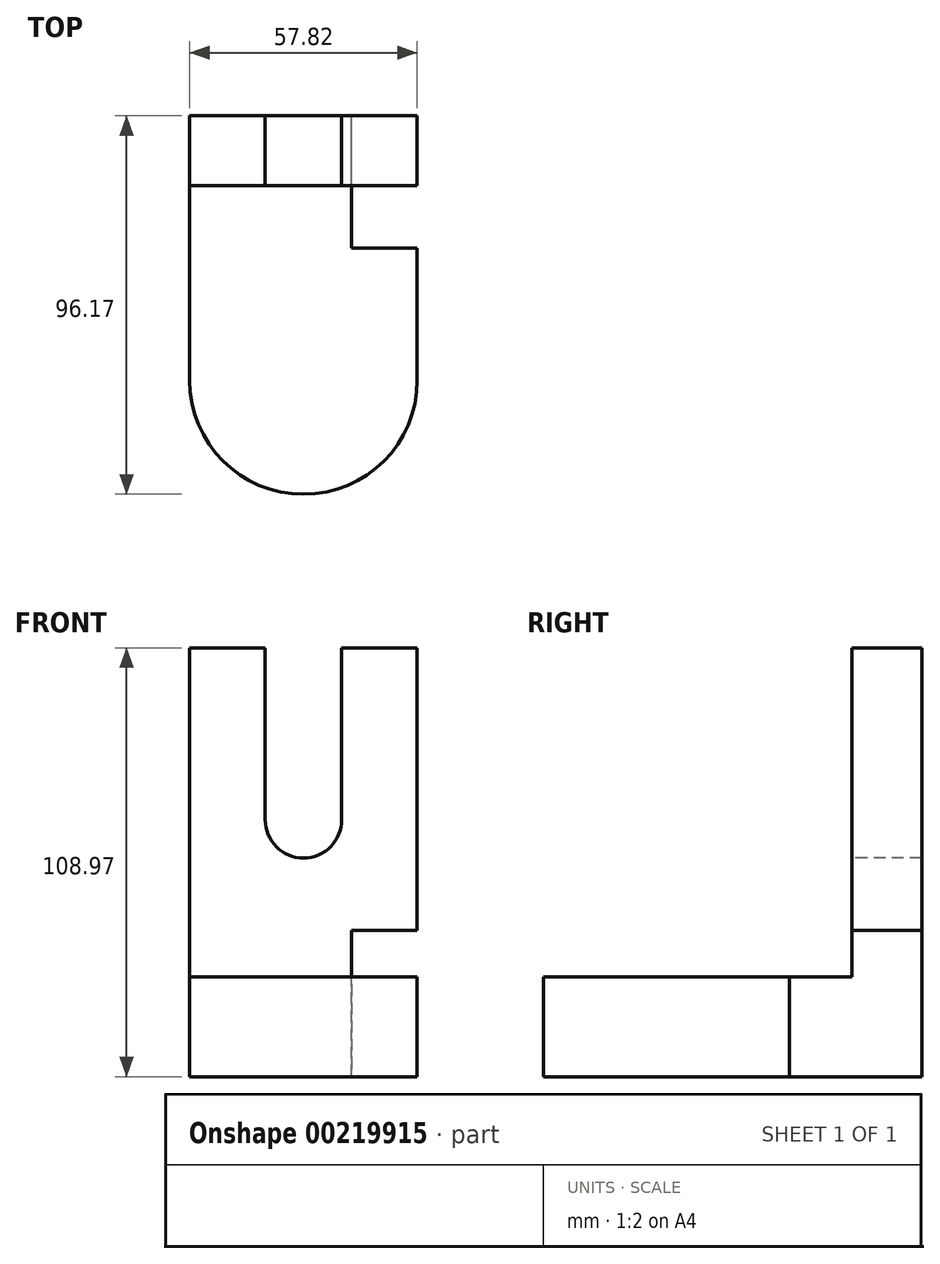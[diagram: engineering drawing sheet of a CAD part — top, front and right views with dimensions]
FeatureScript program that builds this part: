
annotation { "Feature Type Name" : "Feature", "Feature Type Description" : "" }
export const myFeature = defineFeature(function(context is Context, id is Id, definition is map)
    precondition{}
    {
        {
            var Q0;
            Q0=qCreatedBy(makeId("Top.planeOp"),FACE);
            var sketch = newSketch(context, id + "F0", { "sketchPlane" : qUnion([Q0])});
            skLineSegment(sketch, "E0.bottom", {"start": v(-28.91, -33.63) * mm, "end": v(28.91, -33.63) * mm});
            skLineSegment(sketch, "E0.top", {"start": v(-28.91, 33.63) * mm, "end": v(28.91, 33.63) * mm});
            skLineSegment(sketch, "E0.left", {"start": v(-28.91, -33.63) * mm, "end": v(-28.91, 33.63) * mm});
            skLineSegment(sketch, "E0.right", {"start": v(28.91, -33.63) * mm, "end": v(28.91, 33.63) * mm});
            skPoint(sketch, "E0.middle", {"position": v(0, 0) * mm});
            skSolve(sketch);
        }
        {
            var Q0;
            Q0 = qSketchRegion(id + "F0", true);
            extrude(context, id + "F1", {"entities" : qUnion([Q0]), "depth" : 25.4 * mm});
        }
        {
            var Q0;
            Q0=makeQuery(id+"F1.opExtrude","CAP_FACE",FACE,{"disambiguationData":[OSD([sQuery(id+"F0.wireOp",EDGE,"E0.bottom"),sQuery(id+"F0.wireOp",EDGE,"E0.top"),sQuery(id+"F0.wireOp",EDGE,"E0.left"),sQuery(id+"F0.wireOp",EDGE,"E0.right")])],"isStart":false});
            var sketch = newSketch(context, id + "F2", { "sketchPlane" : qUnion([Q0])});
            skLineSegment(sketch, "E1.bottom", {"start": v(-28.91, 33.63) * mm, "end": v(28.91, 33.63) * mm});
            skLineSegment(sketch, "E1.top", {"start": v(-28.91, 15.92) * mm, "end": v(28.91, 15.92) * mm});
            skLineSegment(sketch, "E1.left", {"start": v(-28.91, 33.63) * mm, "end": v(-28.91, 15.92) * mm});
            skLineSegment(sketch, "E1.right", {"start": v(28.91, 33.63) * mm, "end": v(28.91, 15.92) * mm});
            skSolve(sketch);
        }
        {
            var Q0;
            Q0 = qSketchRegion(id + "F2", true);
            extrude(context, id + "F3", {"entities" : qUnion([Q0]), "operationType" : NewBodyOperationType.ADD, "depth" : 83.57 * mm});
        }
        {
            var Q0;
            Q0=makeQuery(id+"F3.opExtrude","CAP_FACE",FACE,{"disambiguationData":[OSD([sQuery(id+"F2.wireOp",EDGE,"E1.bottom"),sQuery(id+"F2.wireOp",EDGE,"E1.top"),sQuery(id+"F2.wireOp",EDGE,"E1.left"),sQuery(id+"F2.wireOp",EDGE,"E1.right")])],"isStart":false});
            var sketch = newSketch(context, id + "F4", { "sketchPlane" : qUnion([Q0])});
            skLineSegment(sketch, "E2.bottom", {"start": v(9.72, 15.92) * mm, "end": v(-9.72, 15.92) * mm});
            skLineSegment(sketch, "E2.top", {"start": v(9.72, 36.73) * mm, "end": v(-9.72, 36.73) * mm});
            skLineSegment(sketch, "E2.left", {"start": v(9.72, 15.92) * mm, "end": v(9.72, 36.73) * mm});
            skLineSegment(sketch, "E2.right", {"start": v(-9.72, 15.92) * mm, "end": v(-9.72, 36.73) * mm});
            skPoint(sketch, "E2.middle", {"position": v(0, 26.32) * mm});
            skPoint(sketch, "E2.middle.positionSnap0", {"position": v(0, 15.92) * mm});
            skPoint(sketch, "E2.centerSnap0", {"position": v(0, 15.92) * mm});
            skSolve(sketch);
        }
        {
            var Q0;
            Q0 = qSketchRegion(id + "F4", true);
            extrude(context, id + "F5", {"entities" : qUnion([Q0]), "operationType" : NewBodyOperationType.REMOVE, "oppositeDirection" : true, "depth" : 43.69 * mm});
        }
        {
            var Q0;
            Q0=makeQuery(id+"F3.opExtrude","SWEPT_FACE",FACE,{"disambiguationData":[OSD([sQuery(id+"F2.wireOp",EDGE,"E1.top")])]});
            var sketch = newSketch(context, id + "F6", { "sketchPlane" : qUnion([Q0])});
            skCircle(sketch, "E3", {"center": v(0, 65.28) * mm, "radius": 9.72 * mm});
            skSolve(sketch);
        }
        {
            var Q0;
            Q0 = qSketchRegion(id + "F6", true);
            extrude(context, id + "F7", {"entities" : qUnion([Q0]), "operationType" : NewBodyOperationType.REMOVE, "oppositeDirection" : true, "depth" : 25.4 * mm});
        }
        {
            var Q0;
            Q0=makeQuery(id+"F3.boolean.opBoolean","MERGE",FACE,{"derivedFrom":[makeQuery(id+"F1.opExtrude","SWEPT_FACE",FACE,{"disambiguationData":[OSD([sQuery(id+"F0.wireOp",EDGE,"E0.right")])]}),makeQuery(id+"F3.opExtrude","SWEPT_FACE",FACE,{"disambiguationData":[OSD([sQuery(id+"F2.wireOp",EDGE,"E1.right")])]})]});
            var sketch = newSketch(context, id + "F8", { "sketchPlane" : qUnion([Q0])});
            skLineSegment(sketch, "E4", {"start": v(0, 25.4) * mm, "end": v(15.92, 25.4) * mm});
            skLineSegment(sketch, "E5", {"start": v(15.92, 25.4) * mm, "end": v(15.92, 37.2) * mm});
            skLineSegment(sketch, "E6", {"start": v(15.92, 37.2) * mm, "end": v(33.63, 37.2) * mm});
            skLineSegment(sketch, "E7", {"start": v(33.63, 37.2) * mm, "end": v(33.63, 0) * mm});
            skLineSegment(sketch, "E8", {"start": v(33.63, 0) * mm, "end": v(0, 0) * mm});
            skLineSegment(sketch, "E9", {"start": v(0, 0) * mm, "end": v(0, 25.4) * mm});
            skSolve(sketch);
        }
        {
            var Q0;
            Q0 = qSketchRegion(id + "F8", true);
            extrude(context, id + "F9", {"entities" : qUnion([Q0]), "operationType" : NewBodyOperationType.REMOVE, "oppositeDirection" : true, "depth" : 16.76 * mm});
        }
        {
            var Q0;
            Q0=makeQuery(id+"F1.opExtrude","CAP_FACE",FACE,{"disambiguationData":[OSD([sQuery(id+"F0.wireOp",EDGE,"E0.bottom"),sQuery(id+"F0.wireOp",EDGE,"E0.top"),sQuery(id+"F0.wireOp",EDGE,"E0.left"),sQuery(id+"F0.wireOp",EDGE,"E0.right")])],"isStart":true});
            var sketch = newSketch(context, id + "F10", { "sketchPlane" : qUnion([Q0])});
            skCircle(sketch, "E10", {"center": v(0, 33.63) * mm, "radius": 28.91 * mm});
            skSolve(sketch);
        }
        {
            var Q0;
            Q0 = qSketchRegion(id + "F10", true);
            extrude(context, id + "F11", {"entities" : qUnion([Q0]), "operationType" : NewBodyOperationType.ADD, "oppositeDirection" : true, "depth" : 25.4 * mm});
        }
    });
